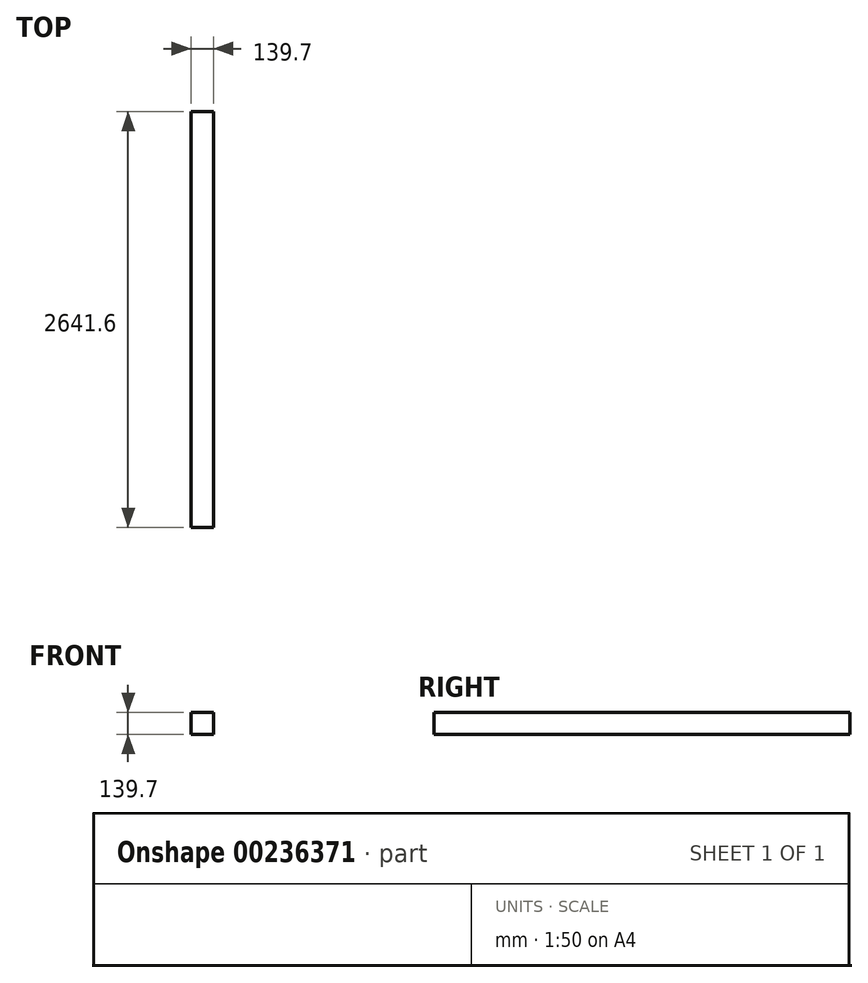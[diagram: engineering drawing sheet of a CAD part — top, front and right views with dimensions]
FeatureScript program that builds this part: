
annotation { "Feature Type Name" : "Feature", "Feature Type Description" : "" }
export const myFeature = defineFeature(function(context is Context, id is Id, definition is map)
    precondition{}
    {
        {
            var Q0;
            Q0=qCreatedBy(makeId("Front.planeOp"),FACE);
            var sketch = newSketch(context, id + "F0", { "sketchPlane" : qUnion([Q0])});
            skLineSegment(sketch, "E0.bottom", {"start": v(-62.89, 76.96) * mm, "end": v(76.81, 76.96) * mm});
            skLineSegment(sketch, "E0.top", {"start": v(-62.89, -62.74) * mm, "end": v(76.81, -62.74) * mm});
            skLineSegment(sketch, "E0.left", {"start": v(-62.89, 76.96) * mm, "end": v(-62.89, -62.74) * mm});
            skLineSegment(sketch, "E0.right", {"start": v(76.81, 76.96) * mm, "end": v(76.81, -62.74) * mm});
            skSolve(sketch);
        }
        {
            var Q0;
            Q0 = qSketchRegion(id + "F0", true);
            extrude(context, id + "F1", {"entities" : qUnion([Q0]), "depth" : 2641.6 * mm});
        }
    });
